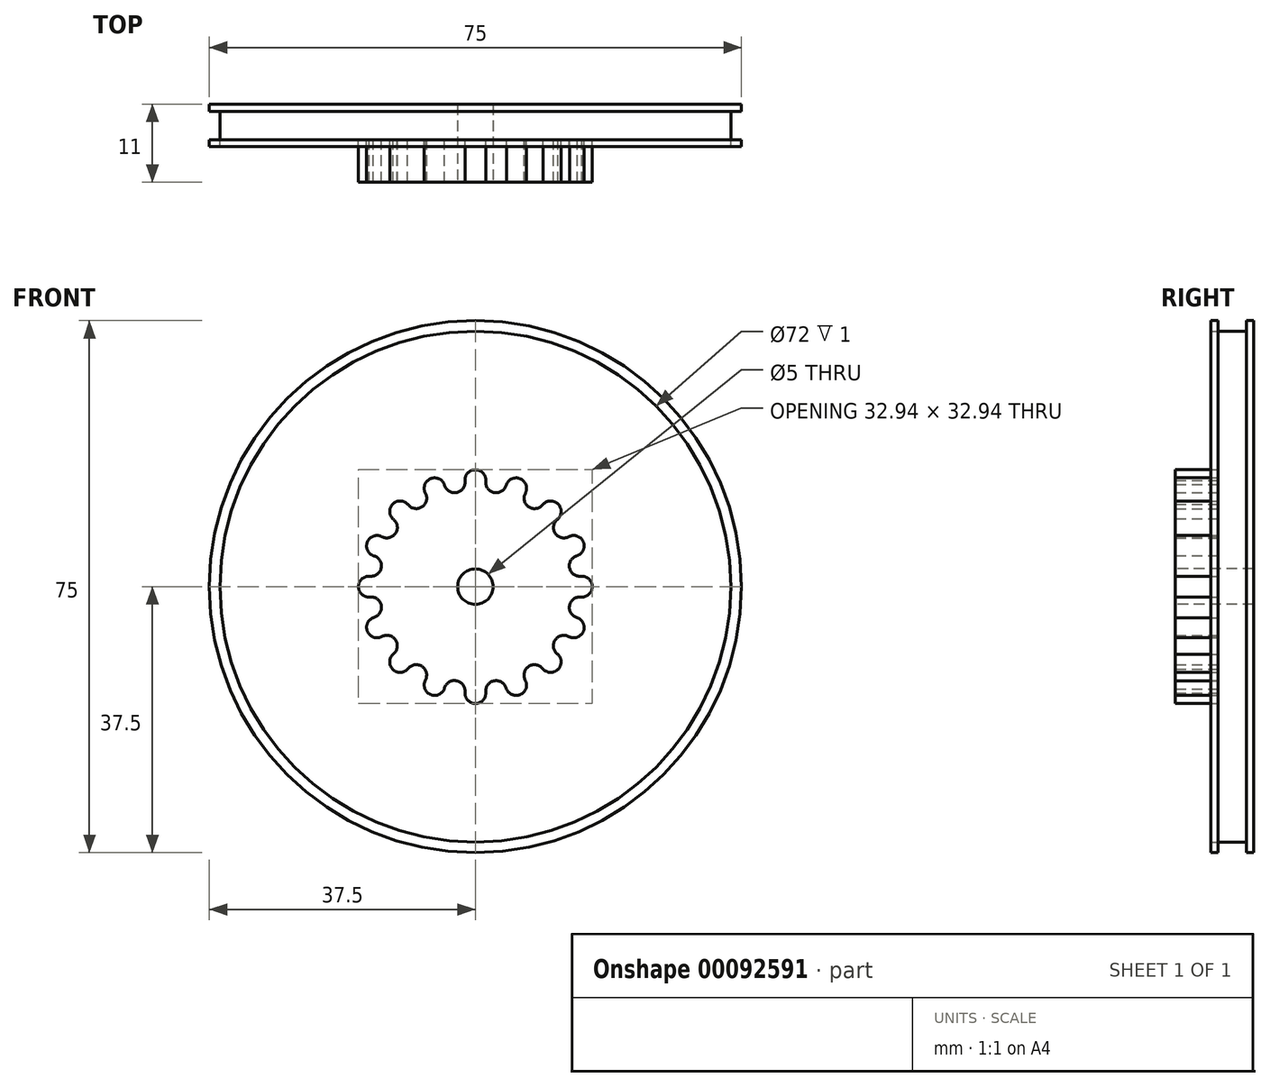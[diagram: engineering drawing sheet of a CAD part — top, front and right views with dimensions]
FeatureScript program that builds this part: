
annotation { "Feature Type Name" : "Feature", "Feature Type Description" : "" }
export const myFeature = defineFeature(function(context is Context, id is Id, definition is map)
    precondition{}
    {
        {
            var Q0;
            Q0=qCreatedBy(makeId("Front.planeOp"),FACE);
            var sketch = newSketch(context, id + "F0", { "sketchPlane" : qUnion([Q0])});
            skCircle(sketch, "E0", {"center": v(0, 0) * mm, "radius": 37.5 * mm});
            skSolve(sketch);
        }
        {
            var Q0;
            Q0=makeQuery(id+"F0.imprint","IMPRINT",FACE,{"disambiguationData":[TD([[makeQuery(id+"F0.imprint","IMPRINT",EDGE,{"derivedFrom":sQuery(id+"F0.wireOp",EDGE,"E0")}),1.0]])]});
            extrude(context, id + "F1", {"entities" : qUnion([Q0]), "depth" : 1 * mm});
        }
        {
            var Q0;
            Q0=makeQuery(id+"F1.opExtrude","CAP_FACE",FACE,{"disambiguationData":[OSD([sQuery(id+"F0.wireOp",EDGE,"E0")])],"isStart":false});
            var sketch = newSketch(context, id + "F2", { "sketchPlane" : qUnion([Q0])});
            skCircle(sketch, "E1", {"center": v(0, 0) * mm, "radius": 36 * mm});
            skSolve(sketch);
        }
        {
            var Q0;
            Q0=makeQuery(id+"F2.imprint","IMPRINT",FACE,{"disambiguationData":[TD([[makeQuery(id+"F2.imprint","IMPRINT",EDGE,{"derivedFrom":sQuery(id+"F2.wireOp",EDGE,"E1")}),1.0]])]});
            extrude(context, id + "F3", {"entities" : qUnion([Q0]), "operationType" : NewBodyOperationType.ADD, "depth" : 4 * mm});
        }
        {
            var Q0;
            Q0=makeQuery(id+"F3.opExtrude","CAP_FACE",FACE,{"disambiguationData":[OSD([sQuery(id+"F2.wireOp",EDGE,"E1")])],"isStart":false});
            var sketch = newSketch(context, id + "F4", { "sketchPlane" : qUnion([Q0])});
            skCircle(sketch, "E2", {"center": v(0, 0) * mm, "radius": 37.5 * mm});
            skSolve(sketch);
        }
        {
            var Q0;
            Q0=makeQuery(id+"F4.imprint","IMPRINT",FACE,{"disambiguationData":[TD([[makeQuery(id+"F4.imprint","IMPRINT",EDGE,{"derivedFrom":sQuery(id+"F4.wireOp",EDGE,"E2")}),1.0]])]});
            extrude(context, id + "F5", {"entities" : qUnion([Q0]), "depth" : 1 * mm});
        }
        {
            var Q0;
            Q0=makeQuery(id+"F3.opExtrude","CAP_FACE",FACE,{"disambiguationData":[OSD([sQuery(id+"F2.wireOp",EDGE,"E1")])],"isStart":false});
            var sketch = newSketch(context, id + "F6", { "sketchPlane" : qUnion([Q0])});
            skArc(sketch, "E3", {"start": v(-11.6, -9.51) * mm, "mid": v(-11.6, -9.51) * mm, "end": v(-11.6, -9.52) * mm});
            skLineSegment(sketch, "E4", {"start": v(0, 0) * mm, "end": v(-15, 0) * mm});
            skArc(sketch, "E5", {"start": v(-14.86, 1.47) * mm, "mid": v(-16.47, 0.04) * mm, "end": v(-14.93, -1.47) * mm});
            skArc(sketch, "E6", {"start": v(-14.86, 1.47) * mm, "mid": v(-13.26, 2.7) * mm, "end": v(-14.4, 4.37) * mm});
            skArc(sketch, "E7.1.0", {"start": v(-14.29, -4.33) * mm, "mid": v(-15.23, -6.27) * mm, "end": v(-13.23, -7.07) * mm});
            skArc(sketch, "E7.1.1", {"start": v(-14.29, -4.33) * mm, "mid": v(-13.28, -2.58) * mm, "end": v(-14.97, -1.47) * mm});
            skArc(sketch, "E7.2.0", {"start": v(-11.54, -9.47) * mm, "mid": v(-11.67, -11.62) * mm, "end": v(-9.52, -11.6) * mm});
            skArc(sketch, "E7.2.1", {"start": v(-11.54, -9.47) * mm, "mid": v(-11.28, -7.46) * mm, "end": v(-13.27, -7.1) * mm});
            skArc(sketch, "E7.3.0", {"start": v(-7.04, -13.16) * mm, "mid": v(-6.34, -15.2) * mm, "end": v(-4.35, -14.35) * mm});
            skArc(sketch, "E7.3.1", {"start": v(-7.04, -13.16) * mm, "mid": v(-7.57, -11.21) * mm, "end": v(-9.55, -11.63) * mm});
            skArc(sketch, "E7.4.0", {"start": v(-1.47, -14.86) * mm, "mid": v(-0.04, -16.47) * mm, "end": v(1.47, -14.93) * mm});
            skArc(sketch, "E7.4.1", {"start": v(-1.47, -14.86) * mm, "mid": v(-2.7, -13.26) * mm, "end": v(-4.37, -14.4) * mm});
            skArc(sketch, "E7.5.0", {"start": v(4.33, -14.29) * mm, "mid": v(6.27, -15.23) * mm, "end": v(7.07, -13.23) * mm});
            skArc(sketch, "E7.5.1", {"start": v(4.33, -14.29) * mm, "mid": v(2.58, -13.28) * mm, "end": v(1.47, -14.97) * mm});
            skArc(sketch, "E7.6.0", {"start": v(9.47, -11.54) * mm, "mid": v(11.62, -11.67) * mm, "end": v(11.6, -9.52) * mm});
            skArc(sketch, "E7.6.1", {"start": v(9.47, -11.54) * mm, "mid": v(7.46, -11.28) * mm, "end": v(7.1, -13.27) * mm});
            skArc(sketch, "E7.7.0", {"start": v(13.16, -7.04) * mm, "mid": v(15.2, -6.34) * mm, "end": v(14.35, -4.35) * mm});
            skArc(sketch, "E7.7.1", {"start": v(13.16, -7.04) * mm, "mid": v(11.21, -7.57) * mm, "end": v(11.63, -9.55) * mm});
            skArc(sketch, "E7.8.0", {"start": v(14.86, -1.47) * mm, "mid": v(16.47, -0.04) * mm, "end": v(14.93, 1.47) * mm});
            skArc(sketch, "E7.8.1", {"start": v(14.86, -1.47) * mm, "mid": v(13.26, -2.7) * mm, "end": v(14.4, -4.37) * mm});
            skArc(sketch, "E7.9.0", {"start": v(14.29, 4.33) * mm, "mid": v(15.23, 6.27) * mm, "end": v(13.23, 7.07) * mm});
            skArc(sketch, "E7.9.1", {"start": v(14.29, 4.33) * mm, "mid": v(13.28, 2.58) * mm, "end": v(14.97, 1.47) * mm});
            skArc(sketch, "E7.10.0", {"start": v(11.54, 9.47) * mm, "mid": v(11.67, 11.62) * mm, "end": v(9.52, 11.6) * mm});
            skArc(sketch, "E7.10.1", {"start": v(11.54, 9.47) * mm, "mid": v(11.28, 7.46) * mm, "end": v(13.27, 7.1) * mm});
            skArc(sketch, "E7.11.0", {"start": v(7.04, 13.16) * mm, "mid": v(6.34, 15.2) * mm, "end": v(4.35, 14.35) * mm});
            skArc(sketch, "E7.11.1", {"start": v(7.04, 13.16) * mm, "mid": v(7.57, 11.21) * mm, "end": v(9.55, 11.63) * mm});
            skArc(sketch, "E7.12.0", {"start": v(1.47, 14.86) * mm, "mid": v(0.06, 16.47) * mm, "end": v(-1.47, 14.97) * mm});
            skArc(sketch, "E7.12.1", {"start": v(1.47, 14.86) * mm, "mid": v(2.7, 13.26) * mm, "end": v(4.37, 14.4) * mm});
            skArc(sketch, "E7.13.0", {"start": v(-4.33, 14.29) * mm, "mid": v(-6.27, 15.23) * mm, "end": v(-7.07, 13.23) * mm});
            skArc(sketch, "E7.13.1", {"start": v(-4.33, 14.29) * mm, "mid": v(-2.58, 13.28) * mm, "end": v(-1.47, 14.97) * mm});
            skArc(sketch, "E7.14.0", {"start": v(-9.47, 11.54) * mm, "mid": v(-11.62, 11.67) * mm, "end": v(-11.6, 9.52) * mm});
            skArc(sketch, "E7.14.1", {"start": v(-9.47, 11.54) * mm, "mid": v(-7.46, 11.28) * mm, "end": v(-7.1, 13.27) * mm});
            skArc(sketch, "E7.15.0", {"start": v(-13.16, 7.04) * mm, "mid": v(-15.2, 6.34) * mm, "end": v(-14.35, 4.35) * mm});
            skArc(sketch, "E7.15.1", {"start": v(-13.16, 7.04) * mm, "mid": v(-11.21, 7.57) * mm, "end": v(-11.63, 9.55) * mm});
            skArc(sketch, "E8.trimOffspring", {"start": v(-9.52, -11.6) * mm, "mid": v(-9.52, -11.6) * mm, "end": v(-9.52, -11.6) * mm});
            skArc(sketch, "E9.trimOffspring", {"start": v(-13.23, -7.07) * mm, "mid": v(-13.23, -7.07) * mm, "end": v(-13.23, -7.07) * mm});
            skPoint(sketch, "E10.orphan", {"position": v(-1.46, 14.93) * mm});
            skPoint(sketch, "E11.orphan", {"position": v(-1.47, 14.93) * mm});
            skPoint(sketch, "E12.orphan", {"position": v(1.47, 14.93) * mm});
            skPoint(sketch, "E13.orphan", {"position": v(4.36, 14.35) * mm});
            skPoint(sketch, "E14.orphan", {"position": v(7.07, 13.23) * mm});
            skPoint(sketch, "E15.orphan", {"position": v(9.52, 11.6) * mm});
            skPoint(sketch, "E16.orphan", {"position": v(11.6, 9.51) * mm});
            skPoint(sketch, "E17.orphan", {"position": v(13.23, 7.07) * mm});
            skPoint(sketch, "E18.orphan", {"position": v(14.36, 4.35) * mm});
            skPoint(sketch, "E19.orphan", {"position": v(14.93, 1.46) * mm});
            skPoint(sketch, "E20.orphan", {"position": v(14.93, -1.47) * mm});
            skPoint(sketch, "E21.orphan", {"position": v(14.35, -4.36) * mm});
            skPoint(sketch, "E22.orphan", {"position": v(13.23, -7.07) * mm});
            skPoint(sketch, "E23.orphan", {"position": v(11.6, -9.52) * mm});
            skPoint(sketch, "E24.orphan", {"position": v(9.51, -11.6) * mm});
            skPoint(sketch, "E25.orphan", {"position": v(7.07, -13.23) * mm});
            skPoint(sketch, "E26.orphan", {"position": v(4.35, -14.36) * mm});
            skPoint(sketch, "E27.orphan", {"position": v(1.46, -14.93) * mm});
            skPoint(sketch, "E28.orphan", {"position": v(-1.47, -14.93) * mm});
            skPoint(sketch, "E29.orphan", {"position": v(-4.36, -14.35) * mm});
            skPoint(sketch, "E30.orphan", {"position": v(-7.07, -13.23) * mm});
            skPoint(sketch, "E31.orphan", {"position": v(-14.36, -4.35) * mm});
            skPoint(sketch, "E32.orphan", {"position": v(-14.93, -1.46) * mm});
            skPoint(sketch, "E33.orphan", {"position": v(-14.93, 1.47) * mm});
            skPoint(sketch, "E34.orphan", {"position": v(-14.35, 4.36) * mm});
            skPoint(sketch, "E35.orphan", {"position": v(-13.23, 7.07) * mm});
            skPoint(sketch, "E36.orphan", {"position": v(-11.6, 9.52) * mm});
            skPoint(sketch, "E37.orphan", {"position": v(-9.51, 11.6) * mm});
            skPoint(sketch, "E38.orphan", {"position": v(-7.07, 13.23) * mm});
            skPoint(sketch, "E39.orphan", {"position": v(-4.35, 14.36) * mm});
            skSolve(sketch);
        }
        {
            var Q0;
            {var subQ11=sQuery(id+"F6.wireOp",EDGE,"E6");Q0=makeQuery(id+"F6.imprint","IMPRINT",FACE,{"disambiguationData":[TD([[makeQuery(id+"F6.imprint","IMPRINT",EDGE,{"derivedFrom":subQ11}),-1.0]])]});}
            extrude(context, id + "F7", {"entities" : qUnion([Q0]), "operationType" : NewBodyOperationType.ADD, "depth" : 6 * mm});
        }
        {
            var Q0;
            Q0=makeQuery(id+"F3.opExtrude","CAP_FACE",FACE,{"disambiguationData":[OSD([sQuery(id+"F2.wireOp",EDGE,"E1")])],"isStart":false});
            extrude(context, id + "F8", {"entities" : qUnion([Q0]), "depth" : 1 * mm});
        }
        {
            var Q0;
            Q0=makeQuery(id+"F7.opExtrude","CAP_FACE",FACE,{"disambiguationData":[OSD([sQuery(id+"F6.wireOp",EDGE,"E5"),sQuery(id+"F6.wireOp",EDGE,"E6"),sQuery(id+"F6.wireOp",EDGE,"E7.1.0"),sQuery(id+"F6.wireOp",EDGE,"E7.1.1"),sQuery(id+"F6.wireOp",EDGE,"E7.2.0"),sQuery(id+"F6.wireOp",EDGE,"E7.2.1"),sQuery(id+"F6.wireOp",EDGE,"E7.3.0"),sQuery(id+"F6.wireOp",EDGE,"E7.3.1"),sQuery(id+"F6.wireOp",EDGE,"E7.4.0"),sQuery(id+"F6.wireOp",EDGE,"E7.4.1"),sQuery(id+"F6.wireOp",EDGE,"E7.5.0"),sQuery(id+"F6.wireOp",EDGE,"E7.5.1"),sQuery(id+"F6.wireOp",EDGE,"E7.6.0"),sQuery(id+"F6.wireOp",EDGE,"E7.6.1"),sQuery(id+"F6.wireOp",EDGE,"E7.7.0"),sQuery(id+"F6.wireOp",EDGE,"E7.7.1"),sQuery(id+"F6.wireOp",EDGE,"E7.8.0"),sQuery(id+"F6.wireOp",EDGE,"E7.8.1"),sQuery(id+"F6.wireOp",EDGE,"E7.9.0"),sQuery(id+"F6.wireOp",EDGE,"E7.9.1"),sQuery(id+"F6.wireOp",EDGE,"E7.10.0"),sQuery(id+"F6.wireOp",EDGE,"E7.10.1"),sQuery(id+"F6.wireOp",EDGE,"E7.11.0"),sQuery(id+"F6.wireOp",EDGE,"E7.11.1"),sQuery(id+"F6.wireOp",EDGE,"E7.12.0"),sQuery(id+"F6.wireOp",EDGE,"E7.12.1"),sQuery(id+"F6.wireOp",EDGE,"E7.13.0"),sQuery(id+"F6.wireOp",EDGE,"E7.13.1"),sQuery(id+"F6.wireOp",EDGE,"E7.14.0"),sQuery(id+"F6.wireOp",EDGE,"E7.14.1"),sQuery(id+"F6.wireOp",EDGE,"E7.15.0"),sQuery(id+"F6.wireOp",EDGE,"E7.15.1")])],"isStart":false});
            var sketch = newSketch(context, id + "F9", { "sketchPlane" : qUnion([Q0])});
            skCircle(sketch, "E40", {"center": v(0, 0) * mm, "radius": 2.5 * mm});
            skSolve(sketch);
        }
        {
            var Q0;
            Q0=makeQuery(id+"F9.imprint","IMPRINT",FACE,{"disambiguationData":[TD([[makeQuery(id+"F9.imprint","IMPRINT",EDGE,{"derivedFrom":sQuery(id+"F9.wireOp",EDGE,"E40")}),1.0]])]});
            extrude(context, id + "F10", {"entities" : qUnion([Q0]), "operationType" : NewBodyOperationType.REMOVE, "oppositeDirection" : true, "depth" : 20 * mm});
        }
    });
